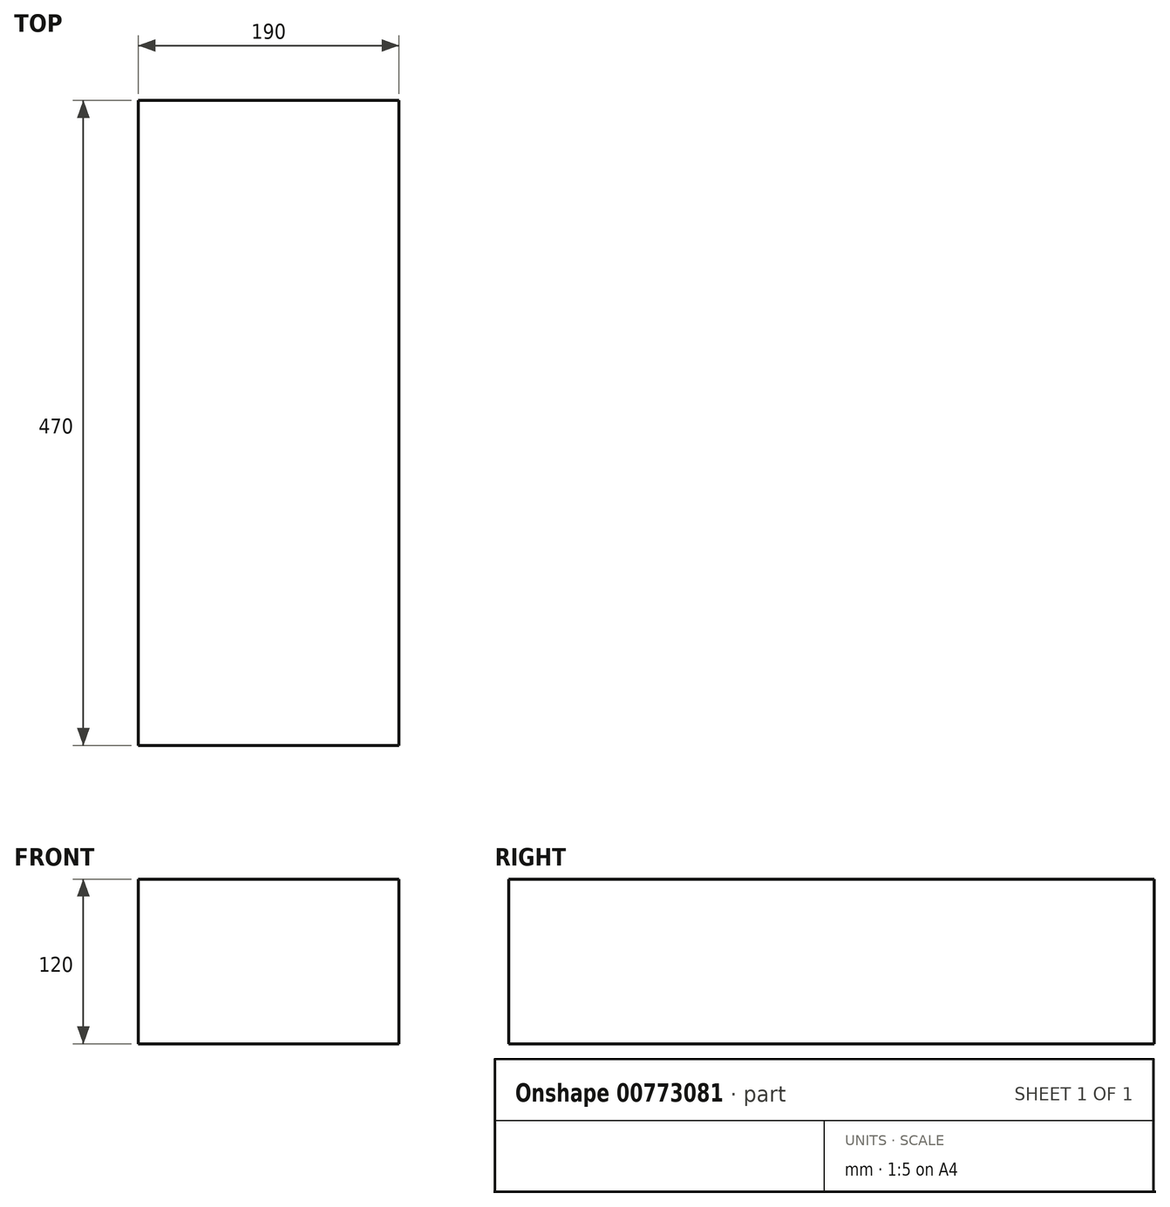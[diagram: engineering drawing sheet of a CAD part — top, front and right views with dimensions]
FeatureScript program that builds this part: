
annotation { "Feature Type Name" : "Feature", "Feature Type Description" : "" }
export const myFeature = defineFeature(function(context is Context, id is Id, definition is map)
    precondition{}
    {
        {
            var Q0;
            Q0=qCreatedBy(makeId("Front.planeOp"),FACE);
            var sketch = newSketch(context, id + "F0", { "sketchPlane" : qUnion([Q0])});
            skLineSegment(sketch, "E0.bottom", {"start": v(-90.64, 73.34) * mm, "end": v(99.36, 73.34) * mm});
            skLineSegment(sketch, "E0.top", {"start": v(-90.64, -46.66) * mm, "end": v(99.36, -46.66) * mm});
            skLineSegment(sketch, "E0.left", {"start": v(-90.64, 73.34) * mm, "end": v(-90.64, -46.66) * mm});
            skLineSegment(sketch, "E0.right", {"start": v(99.36, 73.34) * mm, "end": v(99.36, -46.66) * mm});
            skSolve(sketch);
        }
        {
            var Q0;
            Q0=makeQuery(id+"F0.imprint","IMPRINT",FACE,{"disambiguationData":[TD([[makeQuery(id+"F0.imprint","IMPRINT",EDGE,{"derivedFrom":sQuery(id+"F0.wireOp",EDGE,"E0.bottom")}),-1.0]])]});
            extrude(context, id + "F1", {"entities" : qUnion([Q0]), "depth" : 470 * mm, "offsetDistance" : 25 * mm});
        }
    });
